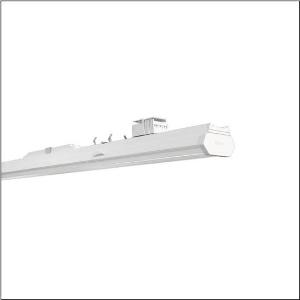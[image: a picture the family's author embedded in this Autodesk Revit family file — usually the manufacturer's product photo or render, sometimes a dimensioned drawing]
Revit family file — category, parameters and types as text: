
# Revit family: licross_r__11_protected_ho_51tp12dn4fxm3s_598f
name_source: partatom
category: Lighting Fixtures
units: mm (PartAtom-declared; Revit-internal decimal feet)

## family parameters
Cut with Voids When Loaded = No
Host = Face
Light Source = No
Part Type = Normal
Room Calculation Point = No
Round Connector Dimension = Use Diameter
Shared = No

## types (1)
- --- (1 x LED, 970 lm, 7.4 W, 4000K)
    Apparent Load = 7 VA
    CIE Flux Codes = 70 91 97 98 100
    Color Rendering = 80
    Color Temperature = 4000K
    Default Elevation = 1800 mm
    Description = Licross® 11 Protected HO, luminaire insert, of sheet steel, galvanised, coil coated, white, length: 1.500mm, width: 90mm, height: 101mm, LED rated luminous flux: 15.270lm, light colour: 840, control gear: DALI 2, with plug, 6-pole, with phase selection, for trunking rail, 14-core, mains connection: 220..240V, AC, 50/60Hz, rated input power: 91W, for trunking rail, 14-core, halogen-free wiring, for emergency light function, converter,control gear: single battery element, battery: LiFeP04, 9Ah, primary light control with lens, of plastic, primary optical cover: cover, of PMMA, light emission: direct distribution, primary light characteristic: symmetric, protection rating (complete): IP64, insulation class (complete): insulation class I (protective earthing), certification: CE, UKCA, protection symbol: D if used in an environment with conductive dust loads with corresponding accessories, impact resistance: IK06, permissible ambient temperature for indoor applications: +5..+30°C, standard: EN 60598-2-22, LABS conformity tested according to VDMA 24364:2018-05, reducing of maximum allowable ambient temperature of 5°C with ceiling mounting, corresponds to IFS (International Featured Standards) requirements for safety and quality in the food industry, packaging unit: 1 piece
    Height = 92 mm
    Lamp = 1 x LED
    Lamp Light Flux = 970 lm
    Lamp Power = 7.4 W
    Lamp count = 1
    Length = 1500 mm
    Luminous efficacy = 131 lm/W
    Manufacturer = Siteco
    ModVariant = No
    Model = 51TP12DN4FXM3S
    Mounting Place = Ceiling
    Mounting Type = Pendant
    Number of Poles = 1
    OnlyDefault = Yes
    Power Factor = 1
    Product Name = Licross® 11 Protected HO
    Product group = luminaire insert
    ProductGroupID = 901
    Protection Class = Protection class I
    Protection Degree = IP 64
    RLX_Detail_Level = 1
    RLX_Emergency_Light_Flux = 0 lm
    RLX_Emergency_Type = 0
    RLX_Emergency_Type_DB = No
    RlxData = <blob elided: 24893 chars, md5=7e08338e>
    Socket = socket
    Standby Power = 0 W
    System Light Flux = 970 lm
    System Power = 7 W
    Type Comments = : emergency light operation: 3 h
    Type Image = l_1256148.jpg
    URL = http://relux.com
    VarID = @adj_041567
    Voltage = 0 V
    Weight = 0.00 kg
    Width = 88 mm

## geometry (parser evidence)
native form markers: Blend x4, Sweep x11
no freeform markers — native parametric forms only
